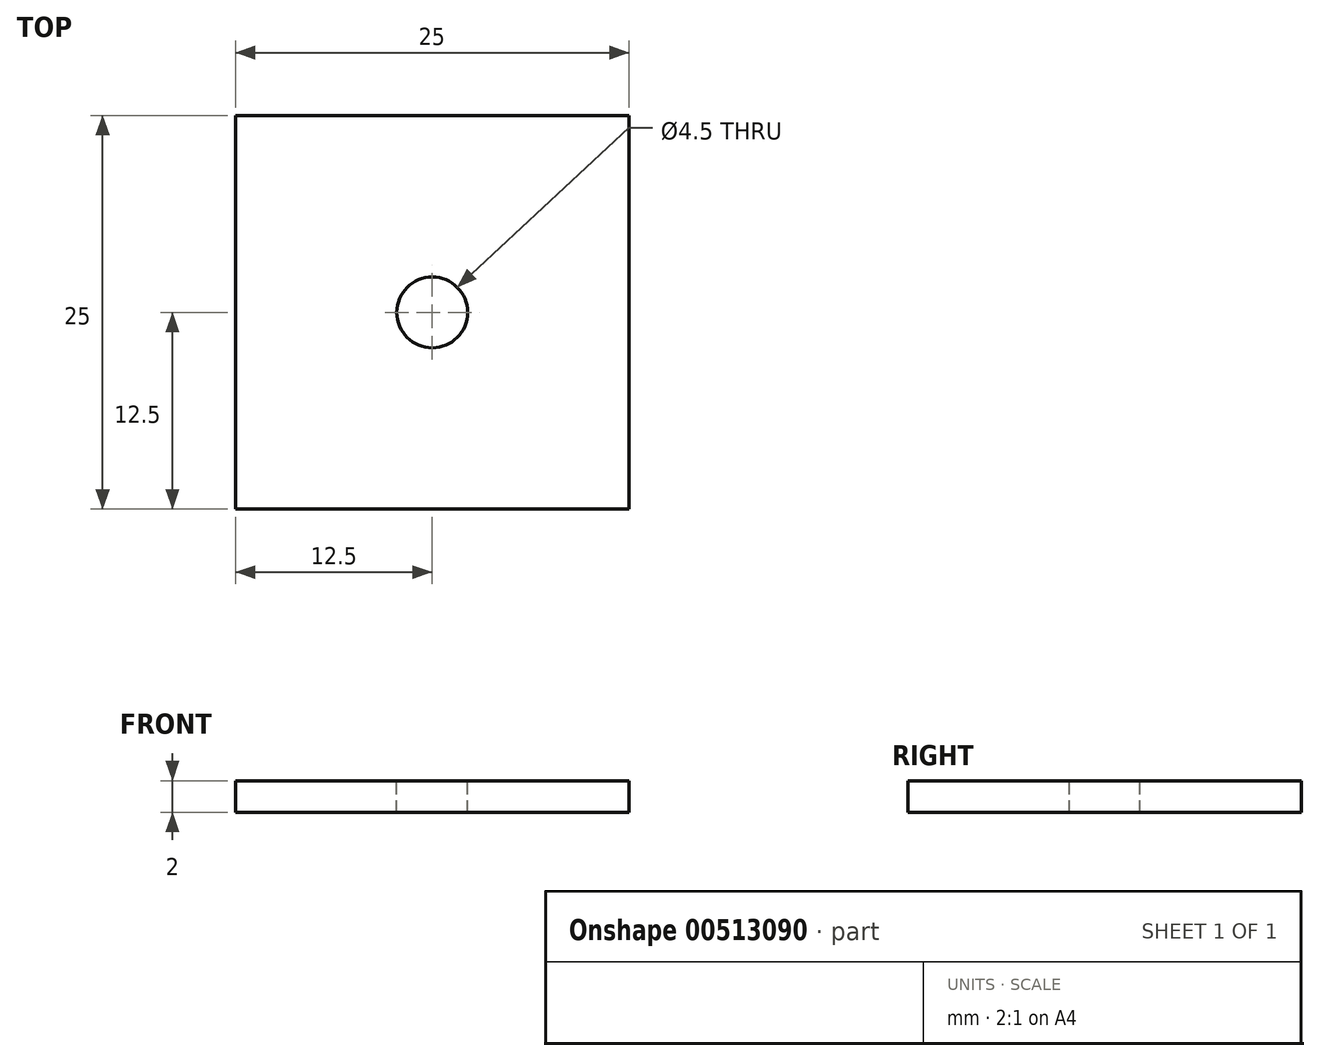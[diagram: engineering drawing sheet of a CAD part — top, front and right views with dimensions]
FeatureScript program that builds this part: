
annotation { "Feature Type Name" : "Feature", "Feature Type Description" : "" }
export const myFeature = defineFeature(function(context is Context, id is Id, definition is map)
    precondition{}
    {
        {
            var Q0;
            Q0=qCreatedBy(makeId("Top.planeOp"),FACE);
            var sketch = newSketch(context, id + "F0", { "sketchPlane" : qUnion([Q0])});
            skLineSegment(sketch, "E0.bottom", {"start": v(12.5, -12.5) * mm, "end": v(-12.5, -12.5) * mm});
            skLineSegment(sketch, "E0.top", {"start": v(12.5, 12.5) * mm, "end": v(-12.5, 12.5) * mm});
            skLineSegment(sketch, "E0.left", {"start": v(12.5, -12.5) * mm, "end": v(12.5, 12.5) * mm});
            skLineSegment(sketch, "E0.right", {"start": v(-12.5, -12.5) * mm, "end": v(-12.5, 12.5) * mm});
            skPoint(sketch, "E0.middle", {"position": v(0, 0) * mm});
            skSolve(sketch);
        }
        {
            var Q0;
            Q0=makeQuery(id+"F0.imprint","IMPRINT",FACE,{"disambiguationData":[TD([[makeQuery(id+"F0.imprint","IMPRINT",EDGE,{"derivedFrom":sQuery(id+"F0.wireOp",EDGE,"E0.bottom")}),-1.0]])]});
            extrude(context, id + "F1", {"entities" : qUnion([Q0]), "depth" : 2 * mm, "offsetDistance" : 25 * mm});
        }
        {
            var Q0;
            Q0=makeQuery(id+"F1.opExtrude","CAP_FACE",FACE,{"disambiguationData":[OSD([sQuery(id+"F0.wireOp",EDGE,"E0.bottom"),sQuery(id+"F0.wireOp",EDGE,"E0.top"),sQuery(id+"F0.wireOp",EDGE,"E0.left"),sQuery(id+"F0.wireOp",EDGE,"E0.right")])],"isStart":false});
            var sketch = newSketch(context, id + "F2", { "sketchPlane" : qUnion([Q0])});
            skCircle(sketch, "E1", {"center": v(0, 0) * mm, "radius": 2.25 * mm});
            skSolve(sketch);
        }
        {
            var Q0;
            Q0=qSketchRegion(id+"F2",true);
            extrude(context, id + "F3", {"entities" : qUnion([Q0]), "operationType" : NewBodyOperationType.REMOVE, "oppositeDirection" : true, "depth" : 2 * mm});
        }
    });
